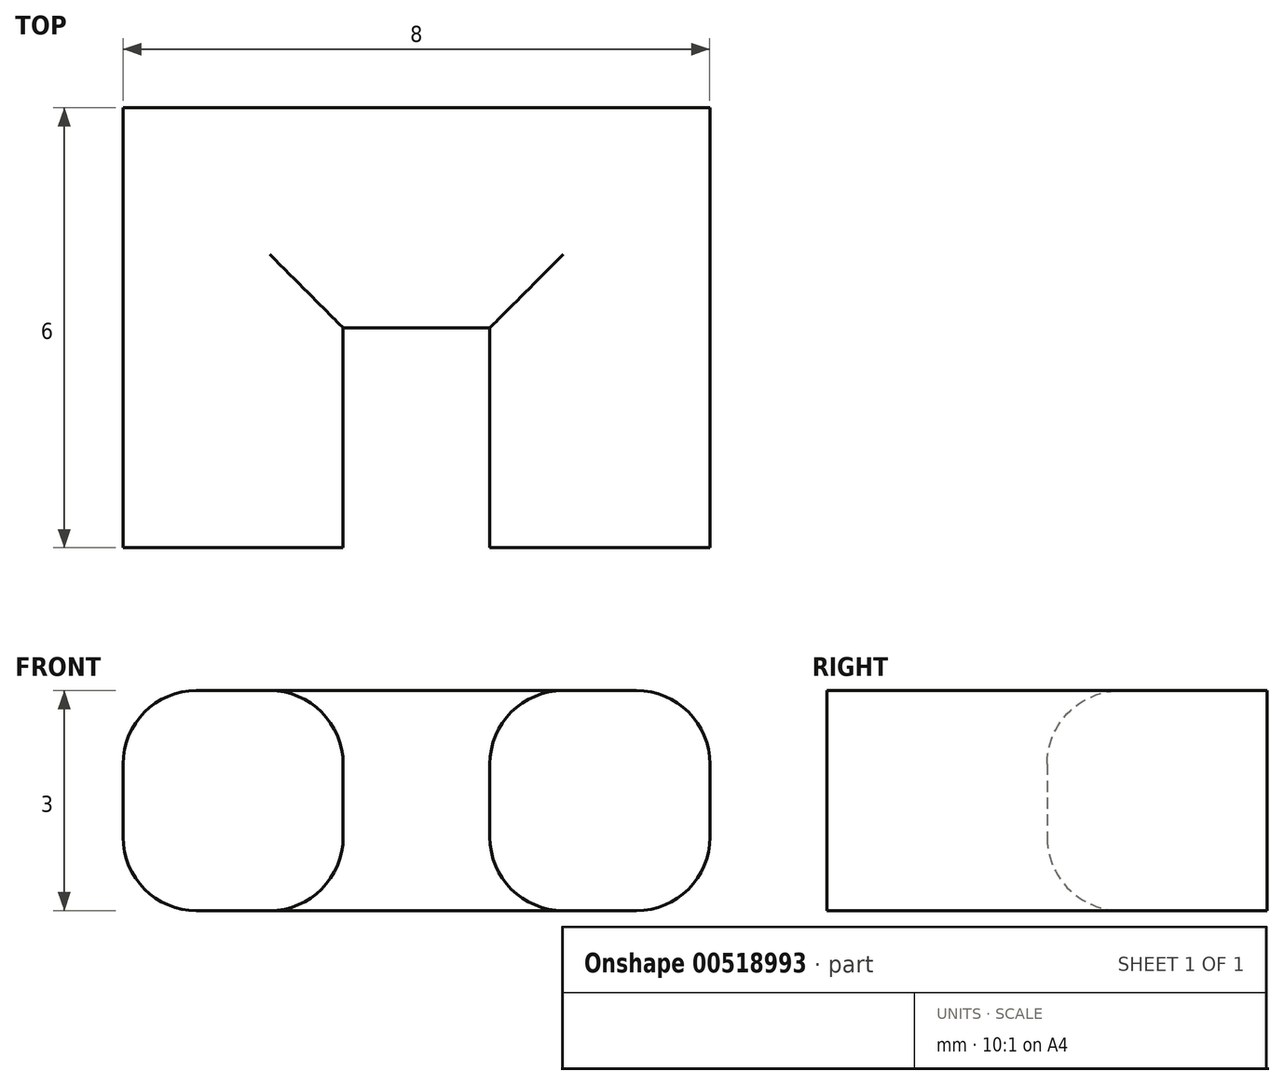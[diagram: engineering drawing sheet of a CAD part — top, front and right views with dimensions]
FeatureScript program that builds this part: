
annotation { "Feature Type Name" : "Feature", "Feature Type Description" : "" }
export const myFeature = defineFeature(function(context is Context, id is Id, definition is map)
    precondition{}
    {
        {
            var Q0;
            Q0=qCreatedBy(makeId("Top.planeOp"),FACE);
            var sketch = newSketch(context, id + "F0", { "sketchPlane" : qUnion([Q0])});
            skLineSegment(sketch, "E0", {"start": v(-8.33, 0) * mm, "end": v(-11.33, 0) * mm});
            skLineSegment(sketch, "E1", {"start": v(-11.33, 0) * mm, "end": v(-11.33, 6) * mm});
            skLineSegment(sketch, "E2", {"start": v(-11.33, 6) * mm, "end": v(-3.33, 6) * mm});
            skLineSegment(sketch, "E3", {"start": v(-3.33, 6) * mm, "end": v(-3.33, 0) * mm});
            skLineSegment(sketch, "E4", {"start": v(-3.33, 0) * mm, "end": v(-6.33, 0) * mm});
            skLineSegment(sketch, "E5", {"start": v(-6.33, 0) * mm, "end": v(-6.33, 3) * mm});
            skLineSegment(sketch, "E6", {"start": v(-6.33, 3) * mm, "end": v(-8.33, 3) * mm});
            skLineSegment(sketch, "E7", {"start": v(-8.33, 3) * mm, "end": v(-8.33, 0) * mm});
            skSolve(sketch);
        }
        {
            var Q0;
            Q0=makeQuery(id+"F0.imprint","IMPRINT",FACE,{"disambiguationData":[TD([[makeQuery(id+"F0.imprint","IMPRINT",EDGE,{"derivedFrom":sQuery(id+"F0.wireOp",EDGE,"E0")}),-1.0]])]});
            extrude(context, id + "F1", {"entities" : qUnion([Q0]), "depth" : 3 * mm, "offsetDistance" : 25 * mm});
        }
        {
            var Q0;
            Q0=makeQuery(id+"F1.opExtrude","CAP_EDGE",EDGE,{"disambiguationData":[OSD([sQuery(id+"F0.wireOp",EDGE,"E5")])],"isStart":false});
            var Q1;
            Q1=makeQuery(id+"F1.opExtrude","CAP_EDGE",EDGE,{"disambiguationData":[OSD([sQuery(id+"F0.wireOp",EDGE,"E6")])],"isStart":false});
            var Q2;
            Q2=makeQuery(id+"F1.opExtrude","CAP_EDGE",EDGE,{"disambiguationData":[OSD([sQuery(id+"F0.wireOp",EDGE,"E7")])],"isStart":false});
            var Q3;
            Q3=makeQuery(id+"F1.opExtrude","CAP_EDGE",EDGE,{"disambiguationData":[OSD([sQuery(id+"F0.wireOp",EDGE,"E6")])],"isStart":true});
            var Q4;
            Q4=makeQuery(id+"F1.opExtrude","CAP_EDGE",EDGE,{"disambiguationData":[OSD([sQuery(id+"F0.wireOp",EDGE,"E7")])],"isStart":true});
            var Q5;
            Q5=makeQuery(id+"F1.opExtrude","CAP_EDGE",EDGE,{"disambiguationData":[OSD([sQuery(id+"F0.wireOp",EDGE,"E5")])],"isStart":true});
            var Q6;
            Q6=makeQuery(id+"F1.opExtrude","CAP_EDGE",EDGE,{"disambiguationData":[OSD([sQuery(id+"F0.wireOp",EDGE,"E1")])],"isStart":true});
            var Q7;
            Q7=makeQuery(id+"F1.opExtrude","CAP_EDGE",EDGE,{"disambiguationData":[OSD([sQuery(id+"F0.wireOp",EDGE,"E1")])],"isStart":false});
            var Q8;
            Q8=makeQuery(id+"F1.opExtrude","CAP_EDGE",EDGE,{"disambiguationData":[OSD([sQuery(id+"F0.wireOp",EDGE,"E3")])],"isStart":false});
            var Q9;
            Q9=makeQuery(id+"F1.opExtrude","CAP_EDGE",EDGE,{"disambiguationData":[OSD([sQuery(id+"F0.wireOp",EDGE,"E3")])],"isStart":true});
            fillet(context, id + "F2", {"entities" : qUnion([Q0, Q1, Q2, Q3, Q4, Q5, Q6, Q7, Q8, Q9]), "radius" : 1 * mm, "tangentPropagation" : true, "allowEdgeOverflow" : false});
        }
    });
